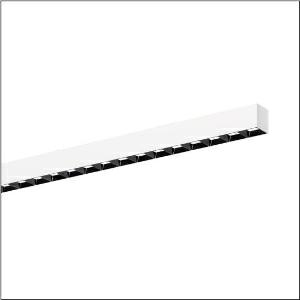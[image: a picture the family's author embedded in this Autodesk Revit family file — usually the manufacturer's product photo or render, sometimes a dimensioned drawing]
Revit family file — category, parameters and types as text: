
# Revit family: silica_r__21_51mx21tat4w_a490
name_source: partatom
category: Lighting Fixtures
units: mm (PartAtom-declared; Revit-internal decimal feet)

## family parameters
Cut with Voids When Loaded = No
Host = Face
Light Source = No
Part Type = Normal
Room Calculation Point = No
Round Connector Dimension = Use Diameter
Shared = No

## types (1)
- --- (1 x LED, 3720 lm, 32.2 W, 6500K)
    Apparent Load = 32 VA
    CIE Flux Codes = 85 99 100 100 100
    Color Rendering = 80
    Color Temperature = 6500K
    Default Elevation = 1800 mm
    Description = Silica® 21, office luminaire, primary light control with darklight reflector, of PMMA, black, CAT 2 (L<= 3000cd/m²), light emission: direct distribution, primary light characteristic: symmetric, installation type: surface-mounted, LED, rated luminous flux: 3.720lm, luminous efficacy: 110lm/W, light colour: 8tw, colour temperature: 2700..6500K, control gear: ECG DALI, with terminal, 3+2-pole, max. 2.5mm², mains connection: 220..240V, AC, 50/60Hz, rated input power: 33.8W, luminaire housing, of aluminium, traffic white (RAL 9016), length: 1.204mm, width: 53mm, height: 53mm, protection rating (complete): IP20, insulation class (complete): insulation class I (protective earthing), certification: CE, permissible operating ambient temperature: 0..+35°C, standard: EN 50419, packaging unit: 1 piece
    Height = 0 mm  [stored 0 ft]
    Lamp = 1 x LED
    Lamp Light Flux = 3720 lm
    Lamp Power = 32.2 W
    Lamp count = 1
    Length = 1204 mm
    Luminous efficacy = 116 lm/W
    Manufacturer = Siteco
    ModVariant = No
    Model = 51MX21TAT4W
    Mounting Place = Ceiling
    Mounting Type = Recessed
    Number of Poles = 1
    OnlyDefault = Yes
    Power Factor = 1
    Product Name = Silica® 21
    Product group = office luminaire | ceiling recessed
    ProductGroupID = 401
    Protection Class = Protection class I
    Protection Degree = IP 20
    RLX_Detail_Level = 1
    RLX_Emergency_Light_Flux = 0 lm
    RLX_Emergency_Type = 0
    RLX_Emergency_Type_DB = No
    RlxData = <blob elided: 38101 chars, md5=b5816366>
    Socket = socket
    Standby Power = 0 W
    System Light Flux = 3720 lm
    System Power = 32 W
    Type Comments = individual setting
    Type Image = l_1313592.jpg
    URL = http://relux.com
    VarID = @adj_089457
    Voltage = 0 V
    Weight = 0.00 kg
    Width = 53 mm

note: [stored X ft] marks values corroborated as IEEE doubles in the binary element streams (Revit-internal decimal feet)

## geometry (parser evidence)
native form markers: Blend x4, Sweep x11
no freeform markers — native parametric forms only
